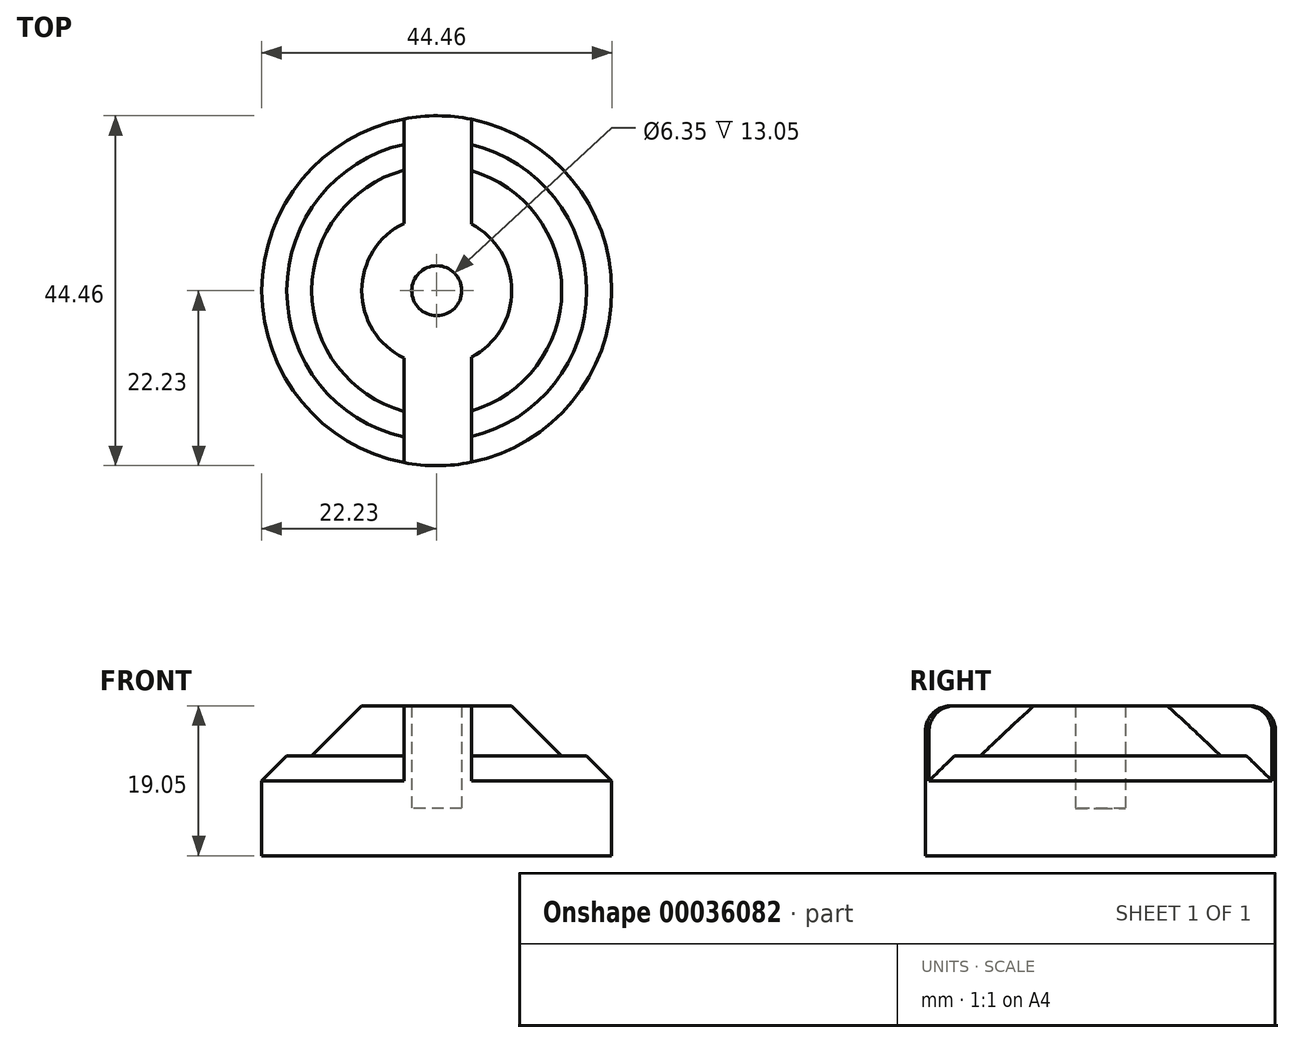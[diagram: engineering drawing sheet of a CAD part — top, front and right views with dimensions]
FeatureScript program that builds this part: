
annotation { "Feature Type Name" : "Feature", "Feature Type Description" : "" }
export const myFeature = defineFeature(function(context is Context, id is Id, definition is map)
    precondition{}
    {
        {
            var Q0;
            Q0=qCreatedBy(makeId("Top.planeOp"),FACE);
            var sketch = newSketch(context, id + "F0", { "sketchPlane" : qUnion([Q0])});
            skCircle(sketch, "E0", {"center": v(0, 0) * mm, "radius": 22.23 * mm});
            skCircle(sketch, "E1", {"center": v(0, 0) * mm, "radius": 3.18 * mm});
            skCircle(sketch, "E2", {"center": v(0, 0) * mm, "radius": 12.7 * mm});
            skLineSegment(sketch, "E3", {"start": v(0, 22.23) * mm, "end": v(0, -22.23) * mm, "construction": true});
            skLineSegment(sketch, "E4", {"start": v(-4.18, 21.83) * mm, "end": v(-4.18, -21.83) * mm});
            skLineSegment(sketch, "E5", {"start": v(4.4, 21.79) * mm, "end": v(4.4, -21.79) * mm});
            skSolve(sketch);
        }
        {
            var Q0;
            Q0 = qSketchRegion(id + "F0", true);
            var Q1;
            {var subQ0=sQuery(id+"F0.wireOp",EDGE,"E4");var subQ1=sQuery(id+"F0.wireOp",EDGE,"E2");var subQ3=makeQuery(id+"F0.imprint","INTERSECT",VERTEX,{"disambiguationData":[OD(0.0)],"derivedFrom":[subQ1,subQ0]});Q1=makeQuery(id+"F0.imprint","IMPRINT",FACE,{"disambiguationData":[TD([[makeQuery(id+"F0.imprint","IMPRINT",EDGE,{"disambiguationData":[TD([[subQ3,-1.0]])],"derivedFrom":subQ1}),1.0]])]});}
            var Q2;
            {var subQ0=sQuery(id+"F0.wireOp",EDGE,"E3");var subQ1=sQuery(id+"F0.wireOp",EDGE,"E1");var subQ3=makeQuery(id+"F0.imprint","INTERSECT",VERTEX,{"disambiguationData":[OD(0.0)],"derivedFrom":[subQ1,subQ0]});Q2=makeQuery(id+"F0.imprint","IMPRINT",FACE,{"disambiguationData":[TD([[makeQuery(id+"F0.imprint","IMPRINT",EDGE,{"disambiguationData":[TD([[subQ3,1.0]])],"derivedFrom":subQ1}),1.0]])]});}
            var Q3;
            {var subQ0=sQuery(id+"F0.wireOp",EDGE,"E3");var subQ1=sQuery(id+"F0.wireOp",EDGE,"E1");var subQ3=makeQuery(id+"F0.imprint","INTERSECT",VERTEX,{"disambiguationData":[OD(0.0)],"derivedFrom":[subQ1,subQ0]});Q3=makeQuery(id+"F0.imprint","IMPRINT",FACE,{"disambiguationData":[TD([[makeQuery(id+"F0.imprint","IMPRINT",EDGE,{"disambiguationData":[TD([[subQ3,-1.0]])],"derivedFrom":subQ1}),1.0]])]});}
            var Q4;
            {var subQ4=sQuery(id+"F0.wireOp",EDGE,"E3");var subQ6=sQuery(id+"F0.wireOp",EDGE,"E1");var subQ9=makeQuery(id+"F0.imprint","INTERSECT",VERTEX,{"disambiguationData":[OD(0.0)],"derivedFrom":[subQ6,subQ4]});Q4=makeQuery(id+"F0.imprint","IMPRINT",FACE,{"disambiguationData":[TD([[makeQuery(id+"F0.imprint","IMPRINT",EDGE,{"disambiguationData":[TD([[subQ9,1.0]])],"derivedFrom":subQ6}),-1.0]])]});}
            var Q5;
            {var subQ0=sQuery(id+"F0.wireOp",EDGE,"E5");var subQ1=sQuery(id+"F0.wireOp",EDGE,"E2");var subQ3=makeQuery(id+"F0.imprint","INTERSECT",VERTEX,{"disambiguationData":[OD(0.0)],"derivedFrom":[subQ1,subQ0]});Q5=makeQuery(id+"F0.imprint","IMPRINT",FACE,{"disambiguationData":[TD([[makeQuery(id+"F0.imprint","IMPRINT",EDGE,{"disambiguationData":[TD([[subQ3,1.0]])],"derivedFrom":subQ1}),1.0]])]});}
            var Q6;
            {var subQ4=sQuery(id+"F0.wireOp",EDGE,"E3");var subQ6=sQuery(id+"F0.wireOp",EDGE,"E1");var subQ9=makeQuery(id+"F0.imprint","INTERSECT",VERTEX,{"disambiguationData":[OD(0.0)],"derivedFrom":[subQ6,subQ4]});Q6=makeQuery(id+"F0.imprint","IMPRINT",FACE,{"disambiguationData":[TD([[makeQuery(id+"F0.imprint","IMPRINT",EDGE,{"disambiguationData":[TD([[subQ9,-1.0]])],"derivedFrom":subQ6}),-1.0]])]});}
            var Q7;
            Q7=makeQuery(id+"F0.imprint","IMPRINT",FACE,{"disambiguationData":[TD([[makeQuery(id+"F0.imprint","IMPRINT",EDGE,{"derivedFrom":sQuery(id+"F0.wireOp",EDGE,"E1")}),-1.0]])]});
            var Q8;
            Q8=makeQuery(id+"F0.imprint","IMPRINT",FACE,{"disambiguationData":[TD([[makeQuery(id+"F0.imprint","IMPRINT",EDGE,{"derivedFrom":sQuery(id+"F0.wireOp",EDGE,"E1")}),1.0]])]});
            extrude(context, id + "F1", {"entities" : qUnion([Q0, Q1, Q2, Q3, Q4, Q5, Q6, Q7, Q8]), "depth" : 12.7 * mm});
        }
        {
            var Q0;
            {var subQ0=sQuery(id+"F0.wireOp",EDGE,"E5");var subQ1=sQuery(id+"F0.wireOp",EDGE,"E2");var subQ3=makeQuery(id+"F0.imprint","INTERSECT",VERTEX,{"disambiguationData":[OD(0.0)],"derivedFrom":[subQ1,subQ0]});Q0=makeQuery(id+"F0.imprint","IMPRINT",FACE,{"disambiguationData":[TD([[makeQuery(id+"F0.imprint","IMPRINT",EDGE,{"disambiguationData":[TD([[subQ3,1.0]])],"derivedFrom":subQ1}),1.0]])]});}
            var Q1;
            {var subQ0=sQuery(id+"F0.wireOp",EDGE,"E4");var subQ1=sQuery(id+"F0.wireOp",EDGE,"E2");var subQ3=makeQuery(id+"F0.imprint","INTERSECT",VERTEX,{"disambiguationData":[OD(0.0)],"derivedFrom":[subQ1,subQ0]});Q1=makeQuery(id+"F0.imprint","IMPRINT",FACE,{"disambiguationData":[TD([[makeQuery(id+"F0.imprint","IMPRINT",EDGE,{"disambiguationData":[TD([[subQ3,-1.0]])],"derivedFrom":subQ1}),1.0]])]});}
            var Q2;
            Q2=makeQuery(id+"F0.imprint","IMPRINT",FACE,{"disambiguationData":[TD([[makeQuery(id+"F0.imprint","IMPRINT",EDGE,{"derivedFrom":sQuery(id+"F0.wireOp",EDGE,"E1")}),-1.0]])]});
            var Q3;
            Q3=makeQuery(id+"F0.imprint","IMPRINT",FACE,{"disambiguationData":[TD([[makeQuery(id+"F0.imprint","IMPRINT",EDGE,{"derivedFrom":sQuery(id+"F0.wireOp",EDGE,"E1")}),1.0]])]});
            extrude(context, id + "F2", {"entities" : qUnion([Q0, Q1, Q2, Q3]), "operationType" : NewBodyOperationType.ADD, "depth" : 19.05 * mm});
        }
        {
            var Q0;
            Q0=makeQuery(id+"F1.opExtrude","CAP_EDGE",EDGE,{"disambiguationData":[OSD([sQuery(id+"F0.wireOp",EDGE,"E0")])],"isStart":false});
            var Q1;
            Q1=makeQuery(id+"F2.boolean.opBoolean","INTERSECT",EDGE,{"derivedFrom":[makeQuery(id+"F1.opExtrude","CAP_FACE",FACE,{"disambiguationData":[OSD([sQuery(id+"F0.wireOp",EDGE,"E0")])],"isStart":false}),makeQuery(id+"F2.opExtrude","SWEPT_FACE",FACE,{"disambiguationData":[OSD([sQuery(id+"F0.wireOp",EDGE,"E2")])]})]});
            var Q2;
            Q2=makeQuery(id+"F2.opExtrude","CAP_EDGE",EDGE,{"disambiguationData":[OSD([sQuery(id+"F0.wireOp",EDGE,"E2")])],"isStart":false});
            chamfer(context, id + "F3", {"entities" : qUnion([Q0, Q1, Q2]), "width" : 3.17 * mm, "tangentPropagation" : true});
        }
        {
            var Q0;
            {var subQ3=sQuery(id+"F0.wireOp",EDGE,"E0");var subQ5=sQuery(id+"F0.wireOp",EDGE,"E4");var subQ7=makeQuery(id+"F0.imprint","INTERSECT",VERTEX,{"disambiguationData":[OD(0.0)],"derivedFrom":[subQ3,subQ5]});Q0=makeQuery(id+"F0.imprint","IMPRINT",FACE,{"disambiguationData":[TD([[makeQuery(id+"F0.imprint","IMPRINT",EDGE,{"disambiguationData":[TD([[subQ7,1.0]])],"derivedFrom":subQ3}),1.0]])]});}
            var Q1;
            Q1=makeQuery(id+"F0.imprint","IMPRINT",FACE,{"disambiguationData":[TD([[makeQuery(id+"F0.imprint","IMPRINT",EDGE,{"derivedFrom":sQuery(id+"F0.wireOp",EDGE,"E1")}),-1.0]])]});
            var Q2;
            {var subQ3=sQuery(id+"F0.wireOp",EDGE,"E0");var subQ5=sQuery(id+"F0.wireOp",EDGE,"E4");var subQ7=makeQuery(id+"F0.imprint","INTERSECT",VERTEX,{"disambiguationData":[OD(1.0)],"derivedFrom":[subQ3,subQ5]});Q2=makeQuery(id+"F0.imprint","IMPRINT",FACE,{"disambiguationData":[TD([[makeQuery(id+"F0.imprint","IMPRINT",EDGE,{"disambiguationData":[TD([[subQ7,-1.0]])],"derivedFrom":subQ3}),1.0]])]});}
            extrude(context, id + "F4", {"entities" : qUnion([Q0, Q1, Q2]), "operationType" : NewBodyOperationType.ADD, "depth" : 19.05 * mm});
        }
        {
            var Q0;
            {var subQ0=sQuery(id+"F0.wireOp",EDGE,"E0");Q0=makeQuery(id+"F4.opExtrude","CAP_EDGE",EDGE,{"disambiguationData":[OSD([subQ0]),TDD([makeQuery(id+"F0.imprint","IMPRINT",EDGE,{"disambiguationData":[TD([[makeQuery(id+"F0.imprint","INTERSECT",VERTEX,{"disambiguationData":[OD(1.0)],"derivedFrom":[subQ0,sQuery(id+"F0.wireOp",EDGE,"E4")]}),-1.0]])],"derivedFrom":subQ0})])],"isStart":false});}
            var Q1;
            {var subQ0=sQuery(id+"F0.wireOp",EDGE,"E0");Q1=makeQuery(id+"F4.opExtrude","CAP_EDGE",EDGE,{"disambiguationData":[OSD([subQ0]),TDD([makeQuery(id+"F0.imprint","IMPRINT",EDGE,{"disambiguationData":[TD([[makeQuery(id+"F0.imprint","INTERSECT",VERTEX,{"disambiguationData":[OD(0.0)],"derivedFrom":[subQ0,sQuery(id+"F0.wireOp",EDGE,"E4")]}),1.0]])],"derivedFrom":subQ0})])],"isStart":false});}
            fillet(context, id + "F5", {"entities" : qUnion([Q0, Q1]), "radius" : 3.17 * mm, "tangentPropagation" : true, "allowEdgeOverflow" : false});
        }
        {
            var Q0;
            Q0=makeQuery(id+"F0.imprint","IMPRINT",FACE,{"disambiguationData":[TD([[makeQuery(id+"F0.imprint","IMPRINT",EDGE,{"derivedFrom":sQuery(id+"F0.wireOp",EDGE,"E1")}),1.0]])]});
            extrude(context, id + "F6", {"entities" : qUnion([Q0]), "operationType" : NewBodyOperationType.REMOVE, "depth" : 21 * mm, "hasSecondDirection" : true, "secondDirectionOppositeDirection" : false, "secondDirectionDepth" : 6 * mm});
        }
    });
